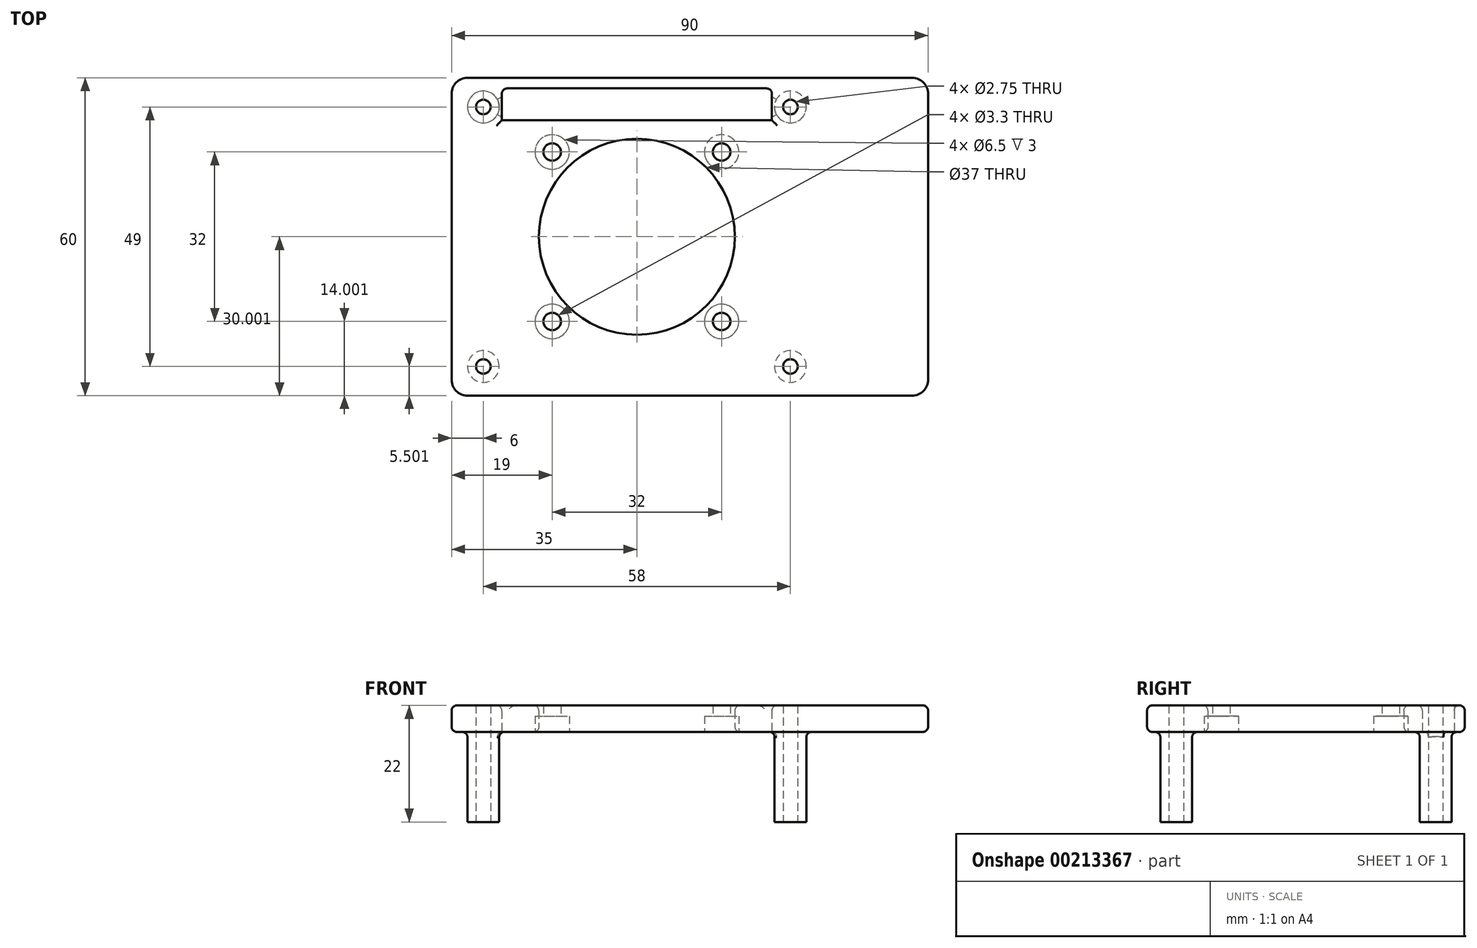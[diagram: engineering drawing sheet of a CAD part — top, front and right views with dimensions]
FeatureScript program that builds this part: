
annotation { "Feature Type Name" : "Feature", "Feature Type Description" : "" }
export const myFeature = defineFeature(function(context is Context, id is Id, definition is map)
    precondition{}
    {
        {
            var Q0;
            Q0=qCreatedBy(makeId("Top.planeOp"),FACE);
            var sketch = newSketch(context, id + "F0", { "sketchPlane" : qUnion([Q0])});
            skLineSegment(sketch, "E0.bottom", {"start": v(-45.78, -37.02) * mm, "end": v(38.22, -37.02) * mm});
            skLineSegment(sketch, "E0.top", {"start": v(-45.78, 22.98) * mm, "end": v(38.22, 22.98) * mm});
            skLineSegment(sketch, "E0.left", {"start": v(-48.78, -34.02) * mm, "end": v(-48.78, 19.98) * mm});
            skLineSegment(sketch, "E0.right", {"start": v(41.22, -34.02) * mm, "end": v(41.22, 19.98) * mm});
            skPoint(sketch, "E1.visualSharp", {"position": v(-48.78, 22.98) * mm});
            skArc(sketch, "E1.filletArc", {"start": v(-45.78, 22.98) * mm, "mid": v(-47.9, 22.1) * mm, "end": v(-48.78, 19.98) * mm});
            skPoint(sketch, "E2.visualSharp", {"position": v(41.22, 22.98) * mm});
            skArc(sketch, "E2.filletArc", {"start": v(41.22, 19.98) * mm, "mid": v(40.34, 22.1) * mm, "end": v(38.22, 22.98) * mm});
            skPoint(sketch, "E3.visualSharp", {"position": v(41.22, -37.02) * mm});
            skArc(sketch, "E3.filletArc", {"start": v(38.22, -37.02) * mm, "mid": v(40.34, -36.14) * mm, "end": v(41.22, -34.02) * mm});
            skPoint(sketch, "E4.visualSharp", {"position": v(-48.78, -37.02) * mm});
            skArc(sketch, "E4.filletArc", {"start": v(-48.78, -34.02) * mm, "mid": v(-47.9, -36.14) * mm, "end": v(-45.78, -37.02) * mm});
            skCircle(sketch, "E5", {"center": v(-42.78, -31.52) * mm, "radius": 1.38 * mm});
            skCircle(sketch, "E6", {"center": v(15.22, -31.52) * mm, "radius": 1.38 * mm});
            skCircle(sketch, "E7", {"center": v(-42.78, 17.48) * mm, "radius": 1.38 * mm});
            skCircle(sketch, "E8", {"center": v(15.22, 17.48) * mm, "radius": 1.38 * mm});
            skCircle(sketch, "E9", {"center": v(-13.78, -7.02) * mm, "radius": 18.5 * mm});
            skLineSegment(sketch, "E10.bottom", {"start": v(6.22, 12.98) * mm, "end": v(-33.78, 12.98) * mm});
            skLineSegment(sketch, "E10.top", {"start": v(6.22, -27.02) * mm, "end": v(-33.78, -27.02) * mm});
            skLineSegment(sketch, "E10.left", {"start": v(6.22, 12.98) * mm, "end": v(6.22, -27.02) * mm});
            skLineSegment(sketch, "E10.right", {"start": v(-33.78, 12.98) * mm, "end": v(-33.78, -27.02) * mm});
            skPoint(sketch, "E11", {"position": v(-29.78, 8.98) * mm});
            skPoint(sketch, "E12", {"position": v(-29.78, -23.02) * mm});
            skPoint(sketch, "E13", {"position": v(2.22, -23.02) * mm});
            skPoint(sketch, "E14", {"position": v(2.22, 8.98) * mm});
            skPoint(sketch, "E15", {"position": v(-13.78, 17.98) * mm});
            skLineSegment(sketch, "E16.bottom", {"start": v(11.72, 20.98) * mm, "end": v(-39.28, 20.98) * mm});
            skLineSegment(sketch, "E16.top", {"start": v(11.72, 14.98) * mm, "end": v(-39.28, 14.98) * mm});
            skLineSegment(sketch, "E16.left", {"start": v(11.72, 20.98) * mm, "end": v(11.72, 14.98) * mm});
            skLineSegment(sketch, "E16.right", {"start": v(-39.28, 20.98) * mm, "end": v(-39.28, 14.98) * mm});
            skSolve(sketch);
        }
        {
            var Q0;
            Q0=makeQuery(id+"F0.imprint","IMPRINT",FACE,{"disambiguationData":[TD([[makeQuery(id+"F0.imprint","IMPRINT",EDGE,{"derivedFrom":sQuery(id+"F0.wireOp",EDGE,"E0.bottom")}),1.0]])]});
            var Q1;
            Q1=makeQuery(id+"F0.imprint","IMPRINT",FACE,{"disambiguationData":[TD([[makeQuery(id+"F0.imprint","IMPRINT",EDGE,{"derivedFrom":sQuery(id+"F0.wireOp",EDGE,"E9")}),-1.0]])]});
            extrude(context, id + "F1", {"entities" : qUnion([Q0, Q1]), "depth" : 5 * mm});
        }
        {
            var Q0;
            Q0=sQuery(id+"F0.wireOp",VERTEX,"E11");
            var Q1;
            Q1=sQuery(id+"F0.wireOp",VERTEX,"E12");
            var Q2;
            Q2=sQuery(id+"F0.wireOp",VERTEX,"E13");
            var Q3;
            Q3=sQuery(id+"F0.wireOp",VERTEX,"E14");
            var Q4;
            Q4=makeQuery(id+"F1.opExtrude","SWEPT_BODY",BODY,{"disambiguationData":[OSD([sQuery(id+"F0.wireOp",EDGE,"E0.bottom"),sQuery(id+"F0.wireOp",EDGE,"E0.top"),sQuery(id+"F0.wireOp",EDGE,"E0.left"),sQuery(id+"F0.wireOp",EDGE,"E0.right"),sQuery(id+"F0.wireOp",EDGE,"E1.filletArc"),sQuery(id+"F0.wireOp",EDGE,"E2.filletArc"),sQuery(id+"F0.wireOp",EDGE,"E3.filletArc"),sQuery(id+"F0.wireOp",EDGE,"E4.filletArc"),sQuery(id+"F0.wireOp",EDGE,"E5"),sQuery(id+"F0.wireOp",EDGE,"E6"),sQuery(id+"F0.wireOp",EDGE,"E7"),sQuery(id+"F0.wireOp",EDGE,"E8"),sQuery(id+"F0.wireOp",EDGE,"E9")])]});
            hole(context, id + "F2", {"style" : HoleStyle.C_BORE, "endStyle" : HoleEndStyle.THROUGH, "oppositeDirection" : true, "standardTappedOrClearance" : lookupTablePath({ "standard" : "ISO", "fit" : "Normal", "size" : "M3", "type" : "Clearance" }), "standardBlindInLast" : lookupTablePath({ "fit" : "Standard", "standard" : "ISO", "size" : "M3", "type" : "Clearance" }), "holeDiameter" : 3.3 * mm, "cBoreDiameter" : 6.5 * mm, "cBoreDepth" : 3 * mm, "locations" : qUnion([Q0, Q1, Q2, Q3]), "scope" : qUnion([Q4]), "isTappedThrough" : true});
        }
        {
            var Q0;
            Q0=makeQuery(id+"F1.opExtrude","CAP_FACE",FACE,{"disambiguationData":[OSD([sQuery(id+"F0.wireOp",EDGE,"E0.bottom"),sQuery(id+"F0.wireOp",EDGE,"E0.top"),sQuery(id+"F0.wireOp",EDGE,"E0.left"),sQuery(id+"F0.wireOp",EDGE,"E0.right"),sQuery(id+"F0.wireOp",EDGE,"E1.filletArc"),sQuery(id+"F0.wireOp",EDGE,"E2.filletArc"),sQuery(id+"F0.wireOp",EDGE,"E3.filletArc"),sQuery(id+"F0.wireOp",EDGE,"E4.filletArc"),sQuery(id+"F0.wireOp",EDGE,"E5"),sQuery(id+"F0.wireOp",EDGE,"E6"),sQuery(id+"F0.wireOp",EDGE,"E7"),sQuery(id+"F0.wireOp",EDGE,"E8"),sQuery(id+"F0.wireOp",EDGE,"E9")])],"isStart":false});
            var sketch = newSketch(context, id + "F3", { "sketchPlane" : qUnion([Q0])});
            skCircle(sketch, "E17", {"center": v(-42.78, 17.48) * mm, "radius": 3 * mm});
            skCircle(sketch, "E18", {"center": v(15.22, 17.48) * mm, "radius": 3 * mm});
            skCircle(sketch, "E19", {"center": v(15.22, -31.52) * mm, "radius": 3 * mm});
            skCircle(sketch, "E20", {"center": v(-42.78, -31.52) * mm, "radius": 3 * mm});
            skSolve(sketch);
        }
        {
            var Q0;
            Q0=makeQuery(id+"F3.imprint","IMPRINT",FACE,{"disambiguationData":[TD([[makeQuery(id+"F3.imprint","IMPRINT",EDGE,{"derivedFrom":sQuery(id+"F3.wireOp",EDGE,"E17")}),1.0]])]});
            var Q1;
            Q1=makeQuery(id+"F3.imprint","IMPRINT",FACE,{"disambiguationData":[TD([[makeQuery(id+"F3.imprint","IMPRINT",EDGE,{"derivedFrom":sQuery(id+"F3.wireOp",EDGE,"E18")}),1.0]])]});
            var Q2;
            Q2=makeQuery(id+"F3.imprint","IMPRINT",FACE,{"disambiguationData":[TD([[makeQuery(id+"F3.imprint","IMPRINT",EDGE,{"derivedFrom":sQuery(id+"F3.wireOp",EDGE,"E19")}),1.0]])]});
            var Q3;
            Q3=makeQuery(id+"F3.imprint","IMPRINT",FACE,{"disambiguationData":[TD([[makeQuery(id+"F3.imprint","IMPRINT",EDGE,{"derivedFrom":sQuery(id+"F3.wireOp",EDGE,"E20")}),1.0]])]});
            extrude(context, id + "F4", {"entities" : qUnion([Q0, Q1, Q2, Q3]), "operationType" : NewBodyOperationType.ADD, "oppositeDirection" : true, "depth" : 22 * mm});
        }
        {
            var Q0;
            Q0=makeQuery(id+"F1.opExtrude","CAP_EDGE",EDGE,{"disambiguationData":[OSD([sQuery(id+"F0.wireOp",EDGE,"E0.bottom")])],"isStart":false});
            var Q1;
            Q1=makeQuery(id+"F1.opExtrude","CAP_EDGE",EDGE,{"disambiguationData":[OSD([sQuery(id+"F0.wireOp",EDGE,"E0.left")])],"isStart":false});
            var Q2;
            Q2=makeQuery(id+"F1.opExtrude","CAP_EDGE",EDGE,{"disambiguationData":[OSD([sQuery(id+"F0.wireOp",EDGE,"E4.filletArc")])],"isStart":false});
            var Q3;
            Q3=makeQuery(id+"F1.opExtrude","CAP_EDGE",EDGE,{"disambiguationData":[OSD([sQuery(id+"F0.wireOp",EDGE,"E3.filletArc")])],"isStart":false});
            var Q4;
            Q4=makeQuery(id+"F1.opExtrude","CAP_EDGE",EDGE,{"disambiguationData":[OSD([sQuery(id+"F0.wireOp",EDGE,"E0.right")])],"isStart":false});
            var Q5;
            Q5=makeQuery(id+"F1.opExtrude","CAP_EDGE",EDGE,{"disambiguationData":[OSD([sQuery(id+"F0.wireOp",EDGE,"E0.top")])],"isStart":false});
            var Q6;
            Q6=makeQuery(id+"F1.opExtrude","CAP_EDGE",EDGE,{"disambiguationData":[OSD([sQuery(id+"F0.wireOp",EDGE,"E2.filletArc")])],"isStart":false});
            var Q7;
            Q7=makeQuery(id+"F1.opExtrude","CAP_EDGE",EDGE,{"disambiguationData":[OSD([sQuery(id+"F0.wireOp",EDGE,"E1.filletArc")])],"isStart":false});
            var Q8;
            Q8=makeQuery(id+"F1.opExtrude","CAP_EDGE",EDGE,{"disambiguationData":[OSD([sQuery(id+"F0.wireOp",EDGE,"E9")])],"isStart":false});
            var Q9;
            Q9=makeQuery(id+"F1.opExtrude","CAP_EDGE",EDGE,{"disambiguationData":[OSD([sQuery(id+"F0.wireOp",EDGE,"E9")])],"isStart":true});
            var Q10;
            Q10=makeQuery(id+"F1.opExtrude","CAP_EDGE",EDGE,{"disambiguationData":[OSD([sQuery(id+"F0.wireOp",EDGE,"E0.left")])],"isStart":true});
            var Q11;
            Q11=makeQuery(id+"F1.opExtrude","CAP_EDGE",EDGE,{"disambiguationData":[OSD([sQuery(id+"F0.wireOp",EDGE,"E4.filletArc")])],"isStart":true});
            var Q12;
            Q12=makeQuery(id+"F4.boolean.opBoolean","INTERSECT",EDGE,{"derivedFrom":[makeQuery(id+"F1.opExtrude","CAP_FACE",FACE,{"disambiguationData":[OSD([sQuery(id+"F0.wireOp",EDGE,"E0.bottom"),sQuery(id+"F0.wireOp",EDGE,"E0.top"),sQuery(id+"F0.wireOp",EDGE,"E0.left"),sQuery(id+"F0.wireOp",EDGE,"E0.right"),sQuery(id+"F0.wireOp",EDGE,"E1.filletArc"),sQuery(id+"F0.wireOp",EDGE,"E2.filletArc"),sQuery(id+"F0.wireOp",EDGE,"E3.filletArc"),sQuery(id+"F0.wireOp",EDGE,"E4.filletArc"),sQuery(id+"F0.wireOp",EDGE,"E5"),sQuery(id+"F0.wireOp",EDGE,"E6"),sQuery(id+"F0.wireOp",EDGE,"E7"),sQuery(id+"F0.wireOp",EDGE,"E8"),sQuery(id+"F0.wireOp",EDGE,"E9")])],"isStart":true}),makeQuery(id+"F4.opExtrude","SWEPT_FACE",FACE,{"disambiguationData":[OSD([sQuery(id+"F3.wireOp",EDGE,"E20")])]})]});
            var Q13;
            Q13=makeQuery(id+"F4.boolean.opBoolean","INTERSECT",EDGE,{"derivedFrom":[makeQuery(id+"F1.opExtrude","CAP_FACE",FACE,{"disambiguationData":[OSD([sQuery(id+"F0.wireOp",EDGE,"E0.bottom"),sQuery(id+"F0.wireOp",EDGE,"E0.top"),sQuery(id+"F0.wireOp",EDGE,"E0.left"),sQuery(id+"F0.wireOp",EDGE,"E0.right"),sQuery(id+"F0.wireOp",EDGE,"E1.filletArc"),sQuery(id+"F0.wireOp",EDGE,"E2.filletArc"),sQuery(id+"F0.wireOp",EDGE,"E3.filletArc"),sQuery(id+"F0.wireOp",EDGE,"E4.filletArc"),sQuery(id+"F0.wireOp",EDGE,"E5"),sQuery(id+"F0.wireOp",EDGE,"E6"),sQuery(id+"F0.wireOp",EDGE,"E7"),sQuery(id+"F0.wireOp",EDGE,"E8"),sQuery(id+"F0.wireOp",EDGE,"E9")])],"isStart":true}),makeQuery(id+"F4.opExtrude","SWEPT_FACE",FACE,{"disambiguationData":[OSD([sQuery(id+"F3.wireOp",EDGE,"E19")])]})]});
            var Q14;
            Q14=makeQuery(id+"F1.opExtrude","CAP_EDGE",EDGE,{"disambiguationData":[OSD([sQuery(id+"F0.wireOp",EDGE,"E0.bottom")])],"isStart":true});
            var Q15;
            Q15=makeQuery(id+"F1.opExtrude","CAP_EDGE",EDGE,{"disambiguationData":[OSD([sQuery(id+"F0.wireOp",EDGE,"E0.right")])],"isStart":true});
            var Q16;
            Q16=makeQuery(id+"F1.opExtrude","CAP_EDGE",EDGE,{"disambiguationData":[OSD([sQuery(id+"F0.wireOp",EDGE,"E3.filletArc")])],"isStart":true});
            var Q17;
            Q17=makeQuery(id+"F1.opExtrude","CAP_EDGE",EDGE,{"disambiguationData":[OSD([sQuery(id+"F0.wireOp",EDGE,"E2.filletArc")])],"isStart":true});
            var Q18;
            Q18=makeQuery(id+"F1.opExtrude","CAP_EDGE",EDGE,{"disambiguationData":[OSD([sQuery(id+"F0.wireOp",EDGE,"E0.top")])],"isStart":true});
            var Q19;
            Q19=makeQuery(id+"F1.opExtrude","CAP_EDGE",EDGE,{"disambiguationData":[OSD([sQuery(id+"F0.wireOp",EDGE,"E1.filletArc")])],"isStart":true});
            var Q20;
            Q20=makeQuery(id+"F4.boolean.opBoolean","INTERSECT",EDGE,{"derivedFrom":[makeQuery(id+"F1.opExtrude","CAP_FACE",FACE,{"disambiguationData":[OSD([sQuery(id+"F0.wireOp",EDGE,"E0.bottom"),sQuery(id+"F0.wireOp",EDGE,"E0.top"),sQuery(id+"F0.wireOp",EDGE,"E0.left"),sQuery(id+"F0.wireOp",EDGE,"E0.right"),sQuery(id+"F0.wireOp",EDGE,"E1.filletArc"),sQuery(id+"F0.wireOp",EDGE,"E2.filletArc"),sQuery(id+"F0.wireOp",EDGE,"E3.filletArc"),sQuery(id+"F0.wireOp",EDGE,"E4.filletArc"),sQuery(id+"F0.wireOp",EDGE,"E5"),sQuery(id+"F0.wireOp",EDGE,"E6"),sQuery(id+"F0.wireOp",EDGE,"E7"),sQuery(id+"F0.wireOp",EDGE,"E8"),sQuery(id+"F0.wireOp",EDGE,"E9")])],"isStart":true}),makeQuery(id+"F4.opExtrude","SWEPT_FACE",FACE,{"disambiguationData":[OSD([sQuery(id+"F3.wireOp",EDGE,"E18")])]})]});
            var Q21;
            Q21=makeQuery(id+"F4.boolean.opBoolean","INTERSECT",EDGE,{"derivedFrom":[makeQuery(id+"F1.opExtrude","CAP_FACE",FACE,{"disambiguationData":[OSD([sQuery(id+"F0.wireOp",EDGE,"E0.bottom"),sQuery(id+"F0.wireOp",EDGE,"E0.top"),sQuery(id+"F0.wireOp",EDGE,"E0.left"),sQuery(id+"F0.wireOp",EDGE,"E0.right"),sQuery(id+"F0.wireOp",EDGE,"E1.filletArc"),sQuery(id+"F0.wireOp",EDGE,"E2.filletArc"),sQuery(id+"F0.wireOp",EDGE,"E3.filletArc"),sQuery(id+"F0.wireOp",EDGE,"E4.filletArc"),sQuery(id+"F0.wireOp",EDGE,"E5"),sQuery(id+"F0.wireOp",EDGE,"E6"),sQuery(id+"F0.wireOp",EDGE,"E7"),sQuery(id+"F0.wireOp",EDGE,"E8"),sQuery(id+"F0.wireOp",EDGE,"E9")])],"isStart":true}),makeQuery(id+"F4.opExtrude","SWEPT_FACE",FACE,{"disambiguationData":[OSD([sQuery(id+"F3.wireOp",EDGE,"E17")])]})]});
            var Q22;
            Q22=makeQuery(id+"F1.opExtrude","CAP_EDGE",EDGE,{"disambiguationData":[OSD([sQuery(id+"F0.wireOp",EDGE,"E16.right")])],"isStart":false});
            var Q23;
            Q23=makeQuery(id+"F1.opExtrude","SWEPT_EDGE",EDGE,{"disambiguationData":[OSD([sQuery(id+"F0.wireOp",EDGE,"E0.top"),sQuery(id+"F0.wireOp",EDGE,"E16.bottom"),sQuery(id+"F0.wireOp",EDGE,"E16.left")])]});
            var Q24;
            Q24=makeQuery(id+"F1.opExtrude","CAP_EDGE",EDGE,{"disambiguationData":[OSD([sQuery(id+"F0.wireOp",EDGE,"E16.left")])],"isStart":false});
            var Q25;
            Q25=makeQuery(id+"F1.opExtrude","CAP_EDGE",EDGE,{"disambiguationData":[OSD([sQuery(id+"F0.wireOp",EDGE,"E16.top")])],"isStart":false});
            var Q26;
            Q26=makeQuery(id+"F1.opExtrude","SWEPT_EDGE",EDGE,{"disambiguationData":[OSD([sQuery(id+"F0.wireOp",EDGE,"E16.bottom"),sQuery(id+"F0.wireOp",EDGE,"E16.right")])]});
            fillet(context, id + "F5", {"entities" : qUnion([Q0, Q1, Q2, Q3, Q4, Q5, Q6, Q7, Q8, Q9, Q10, Q11, Q12, Q13, Q14, Q15, Q16, Q17, Q18, Q19, Q20, Q21, Q22, Q23, Q24, Q25, Q26]), "radius" : 1 * mm, "tangentPropagation" : true, "allowEdgeOverflow" : false});
        }
    });
